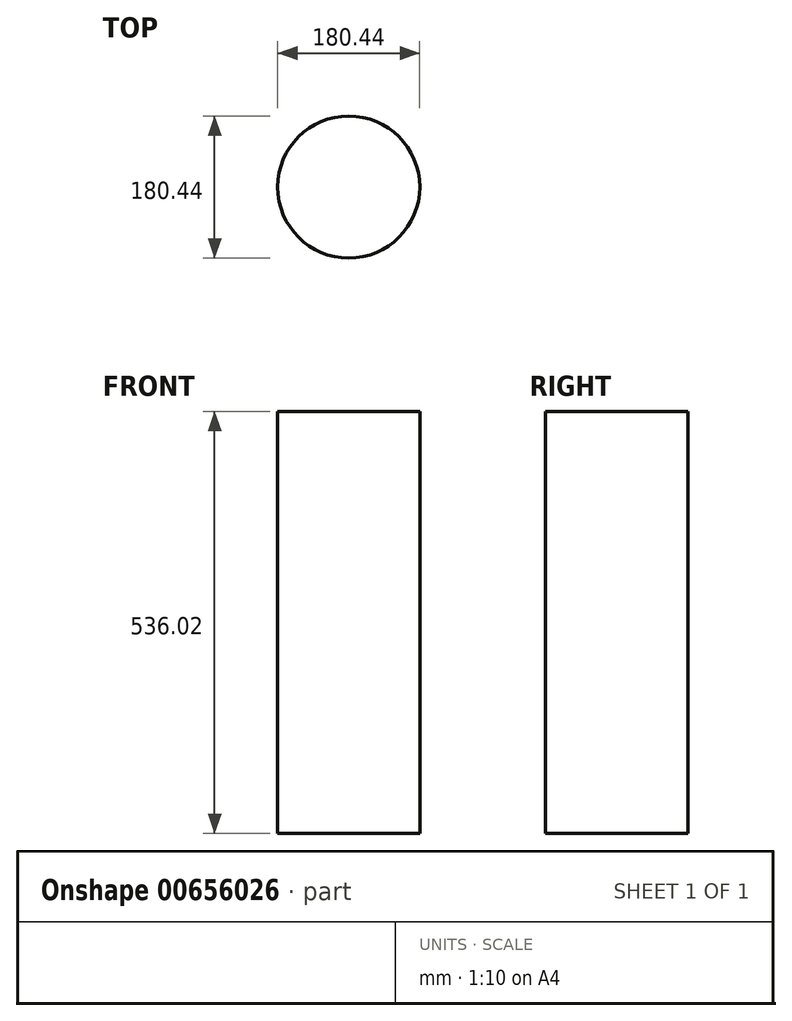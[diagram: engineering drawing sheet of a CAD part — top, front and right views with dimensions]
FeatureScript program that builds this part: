
annotation { "Feature Type Name" : "Feature", "Feature Type Description" : "" }
export const myFeature = defineFeature(function(context is Context, id is Id, definition is map)
    precondition{}
    {
        {
            var Q0;
            Q0=qCreatedBy(makeId("Top.planeOp"),FACE);
            var sketch = newSketch(context, id + "F0", { "sketchPlane" : qUnion([Q0])});
            skCircle(sketch, "E0", {"center": v(0, 0) * mm, "radius": 90.22 * mm});
            skSolve(sketch);
        }
        {
            var Q0;
            Q0=makeQuery(id+"F0.imprint","IMPRINT",FACE,{"disambiguationData":[TD([[makeQuery(id+"F0.imprint","IMPRINT",EDGE,{"derivedFrom":sQuery(id+"F0.wireOp",EDGE,"E0")}),1.0]])]});
            extrude(context, id + "F1", {"entities" : qUnion([Q0]), "depth" : 536.02 * mm, "offsetDistance" : 25.4 * mm});
        }
    });
